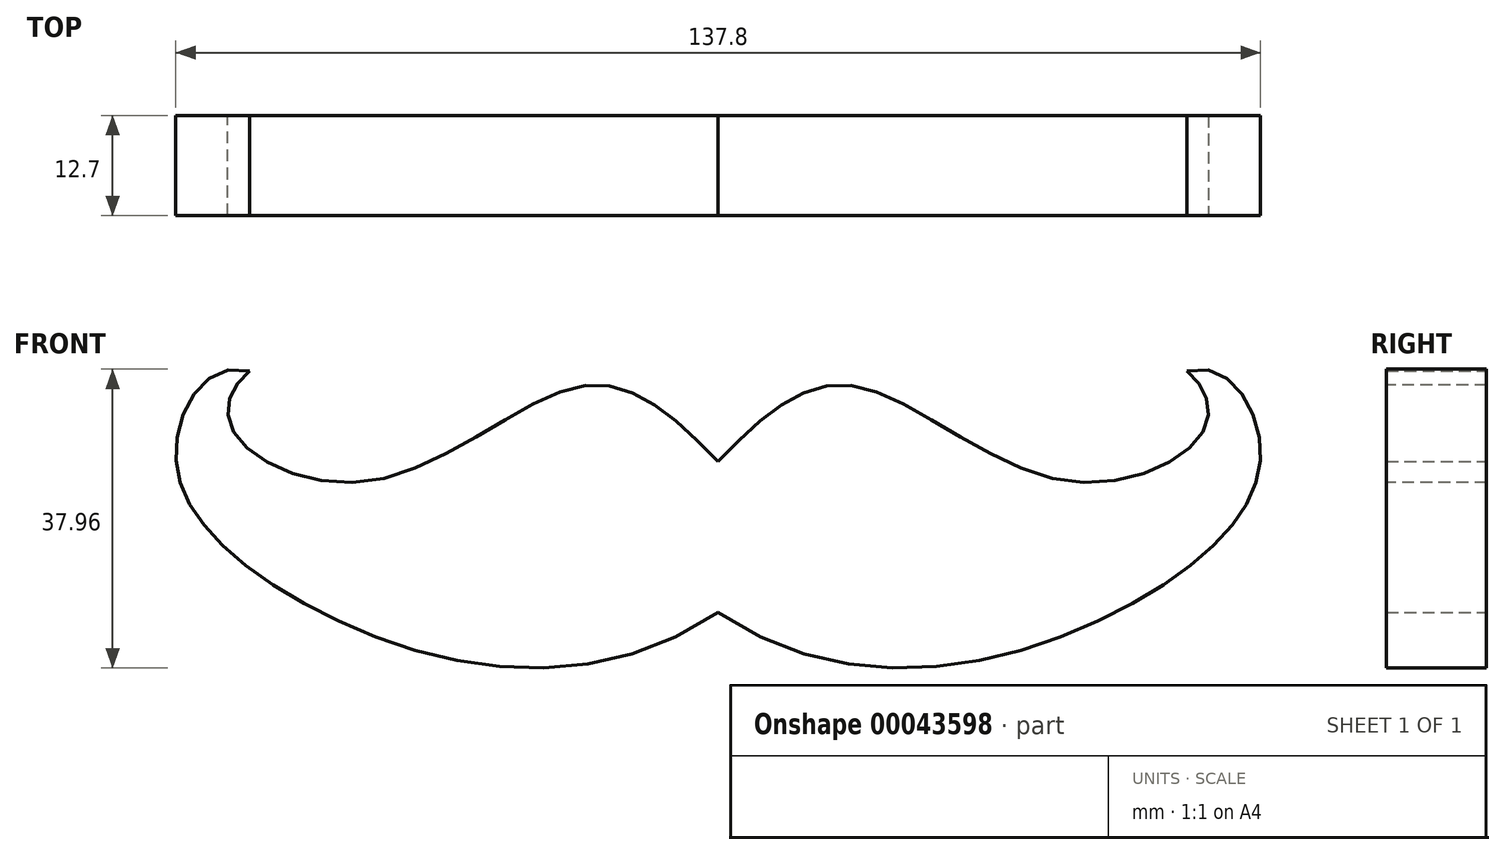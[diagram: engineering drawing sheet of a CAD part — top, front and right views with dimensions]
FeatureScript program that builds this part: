
annotation { "Feature Type Name" : "Feature", "Feature Type Description" : "" }
export const myFeature = defineFeature(function(context is Context, id is Id, definition is map)
    precondition{}
    {
        {
            var Q0;
            Q0=qCreatedBy(makeId("Front.planeOp"),FACE);
            var sketch = newSketch(context, id + "F0", { "sketchPlane" : qUnion([Q0])});
            skFitSpline(sketch, "E0", {"points": [v(0, 0) * mm, v(-16.7, 9.65) * mm, v(-43.8, -2.4) * mm, v(-61.9, 4.4) * mm, v(-59.52, 11.47) * mm], "startDerivative": vector(-61.34, 63.05) * mm, "endDerivative": vector(39.58, 30.07) * mm});
            skFitSpline(sketch, "E1", {"points": [v(0, -19.2) * mm, v(-56.2, -15.9) * mm, v(-68.84, 2.29) * mm, v(-59.52, 11.47) * mm], "startDerivative": vector(-122.07, -82.79) * mm, "endDerivative": vector(66.86, -19.98) * mm});
            skLineSegment(sketch, "E2", {"start": v(0, 0) * mm, "end": v(0, -19.2) * mm, "construction": true});
            skFitSpline(sketch, "E3.MirrorCS", {"points": [v(0, -19.2) * mm, v(56.2, -15.9) * mm, v(68.84, 2.29) * mm, v(59.52, 11.47) * mm], "startDerivative": vector(122.07, -82.79) * mm, "endDerivative": vector(-66.86, -19.98) * mm});
            skFitSpline(sketch, "E4.MirrorCS", {"points": [v(0, 0) * mm, v(16.7, 9.65) * mm, v(43.8, -2.4) * mm, v(61.9, 4.4) * mm, v(59.52, 11.47) * mm], "startDerivative": vector(61.34, 63.05) * mm, "endDerivative": vector(-39.58, 30.07) * mm});
            skSolve(sketch);
        }
        {
            var Q0;
            Q0=makeQuery(id+"F0.imprint","IMPRINT",FACE,{"disambiguationData":[TD([[makeQuery(id+"F0.imprint","IMPRINT",EDGE,{"derivedFrom":sQuery(id+"F0.wireOp",EDGE,"E0")}),1.0]])]});
            extrude(context, id + "F1", {"entities" : qUnion([Q0]), "depth" : 12.7 * mm});
        }
    });
